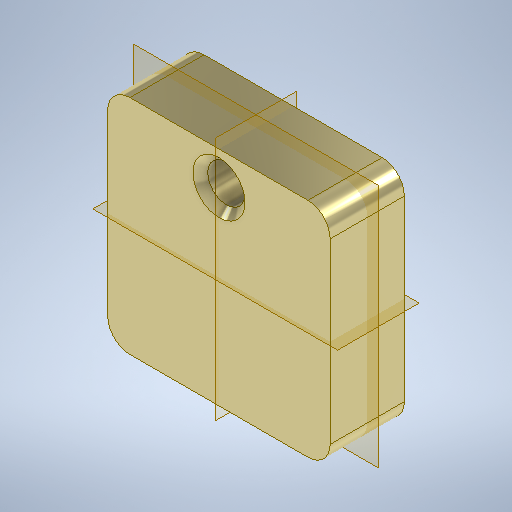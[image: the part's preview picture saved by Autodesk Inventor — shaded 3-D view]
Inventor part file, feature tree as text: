
AUTODESK INVENTOR PART (.ipt)
format: ipt  version: 2025.2 (Build 292293000, 293)  size: 230,912 bytes
history: native  units: mm
features: other x1, extrude x1, fillet x1, chamfer x1, sketch x1
ambient origin geometry x8: Origin, YZ Plane, XZ Plane, XY Plane, X Axis, Y Axis, Z Axis, Center Point
bodies: Body1 (feature_tree)
feature tree (5):
  other  "Sólido1"
  extrude  "Extrusão1"  Depth=10.0mm TaperAngle=0.0deg
  fillet  "Arredondamento1"  Radius=3.0mm
  chamfer  "Chanfro1"  Distance=5.02mm
  sketch  "Esboço1"  dims[d0=30.0mm d1=10.0mm d2=0.0mm d3=3.0mm d4=5.02mm d5=2.0mm d6=1.0mm d7=2.0mm d8=45.0deg]
